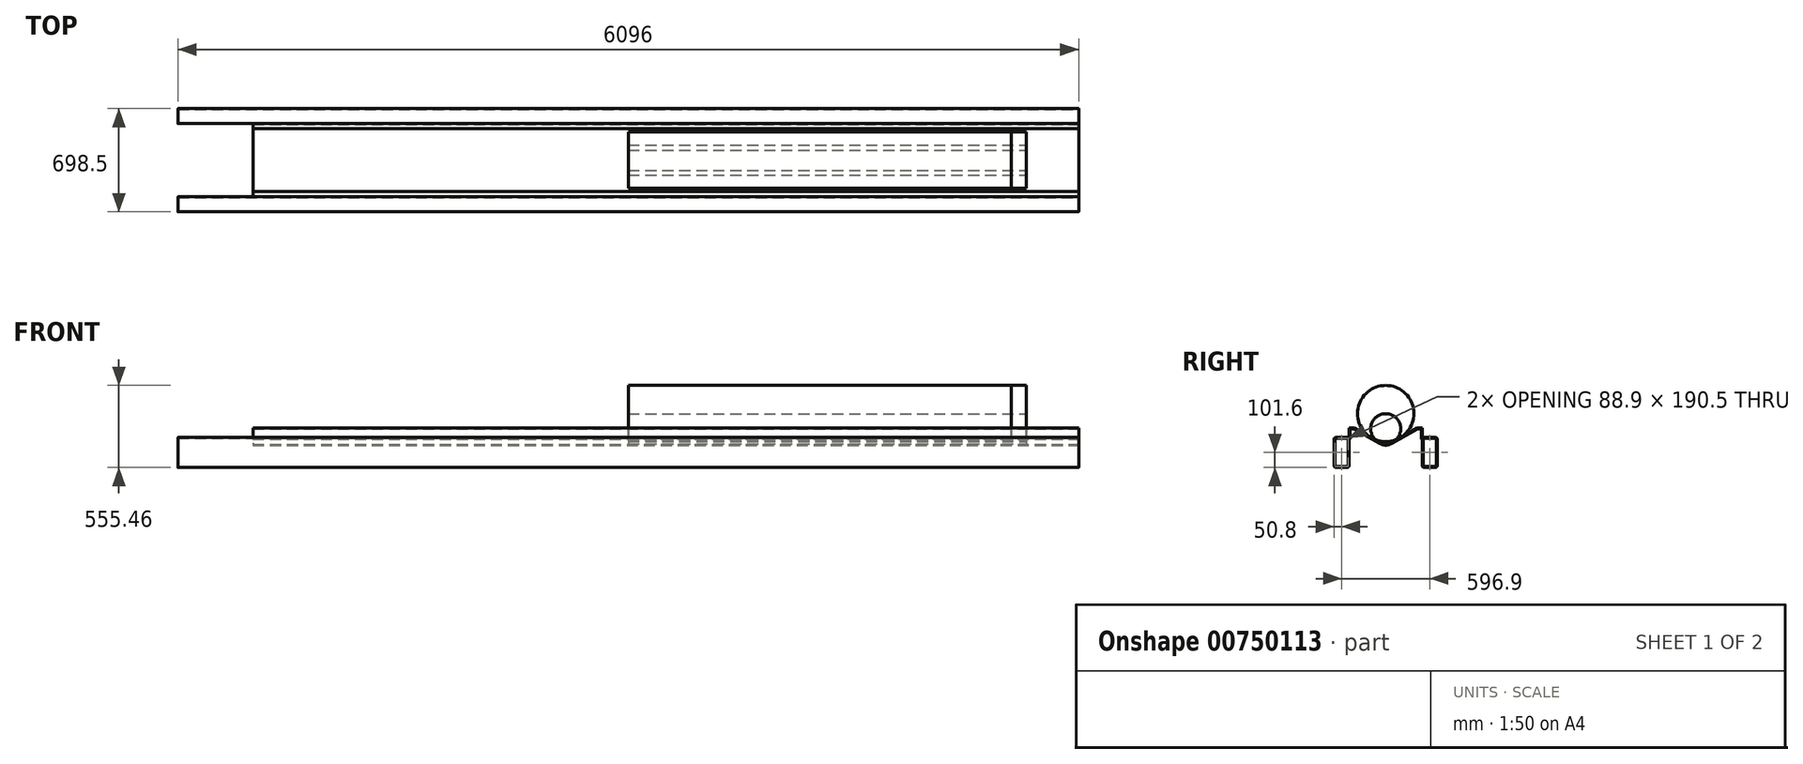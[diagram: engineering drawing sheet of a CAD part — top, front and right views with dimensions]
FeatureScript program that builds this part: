
annotation { "Feature Type Name" : "Feature", "Feature Type Description" : "" }
export const myFeature = defineFeature(function(context is Context, id is Id, definition is map)
    precondition{}
    {
        {
            var Q0;
            Q0=qCreatedBy(makeId("Right.planeOp"),FACE);
            var sketch = newSketch(context, id + "F0", { "sketchPlane" : qUnion([Q0])});
            skPoint(sketch, "E0", {"position": v(0, 0) * mm});
            skLineSegment(sketch, "E1", {"start": v(0, 228.65) * mm, "end": v(0, -305.7) * mm, "construction": true});
            skLineSegment(sketch, "E2.bottom", {"start": v(-336.55, 57.15) * mm, "end": v(-260.35, 57.15) * mm});
            skLineSegment(sketch, "E2.top", {"start": v(-336.55, -146.05) * mm, "end": v(-260.35, -146.05) * mm});
            skLineSegment(sketch, "E2.left", {"start": v(-349.25, 44.45) * mm, "end": v(-349.25, -133.35) * mm});
            skLineSegment(sketch, "E2.right", {"start": v(-247.65, 44.45) * mm, "end": v(-247.65, -133.35) * mm});
            skPoint(sketch, "E3.visualSharp", {"position": v(-247.65, 57.15) * mm});
            skArc(sketch, "E3.filletArc", {"start": v(-247.65, 44.45) * mm, "mid": v(-251.37, 53.43) * mm, "end": v(-260.35, 57.15) * mm});
            skPoint(sketch, "E4.visualSharp", {"position": v(-349.25, -146.05) * mm});
            skArc(sketch, "E4.filletArc", {"start": v(-349.25, -133.35) * mm, "mid": v(-345.53, -142.33) * mm, "end": v(-336.55, -146.05) * mm});
            skPoint(sketch, "E5.visualSharp", {"position": v(-247.65, -146.05) * mm});
            skArc(sketch, "E5.filletArc", {"start": v(-260.35, -146.05) * mm, "mid": v(-251.37, -142.33) * mm, "end": v(-247.65, -133.35) * mm});
            skPoint(sketch, "E6.visualSharp", {"position": v(-349.25, 57.15) * mm});
            skArc(sketch, "E6.filletArc", {"start": v(-336.55, 57.15) * mm, "mid": v(-345.53, 53.43) * mm, "end": v(-349.25, 44.45) * mm});
            skLineSegment(sketch, "E7.MirrorCS", {"start": v(247.65, 44.45) * mm, "end": v(247.65, -133.35) * mm});
            skArc(sketch, "E8.MirrorCS", {"start": v(247.65, 44.45) * mm, "mid": v(251.37, 53.43) * mm, "end": v(260.35, 57.15) * mm});
            skLineSegment(sketch, "E9.MirrorCS", {"start": v(336.55, 57.15) * mm, "end": v(260.35, 57.15) * mm});
            skArc(sketch, "E10.MirrorCS", {"start": v(336.55, 57.15) * mm, "mid": v(345.53, 53.43) * mm, "end": v(349.25, 44.45) * mm});
            skLineSegment(sketch, "E11.MirrorCS", {"start": v(349.25, 44.45) * mm, "end": v(349.25, -133.35) * mm});
            skArc(sketch, "E12.MirrorCS", {"start": v(349.25, -133.35) * mm, "mid": v(345.53, -142.33) * mm, "end": v(336.55, -146.05) * mm});
            skLineSegment(sketch, "E13.MirrorCS", {"start": v(336.55, -146.05) * mm, "end": v(260.35, -146.05) * mm});
            skPoint(sketch, "E14.MirrorP", {"position": v(247.65, -146.05) * mm});
            skArc(sketch, "E15.MirrorCS", {"start": v(260.35, -146.05) * mm, "mid": v(251.37, -142.33) * mm, "end": v(247.65, -133.35) * mm});
            skPoint(sketch, "E16.MirrorP", {"position": v(247.65, 57.15) * mm});
            skLineSegment(sketch, "E17", {"start": v(-213.12, 120.65) * mm, "end": v(-37.54, 21.25) * mm});
            skLineSegment(sketch, "E18.MirrorCS", {"start": v(213.12, 120.65) * mm, "end": v(37.54, 21.25) * mm});
            skLineSegment(sketch, "E19", {"start": v(-364.25, 120.65) * mm, "end": v(0, 120.65) * mm, "construction": true});
            skCircle(sketch, "E20", {"center": v(0, 218.9) * mm, "radius": 190.5 * mm});
            skArc(sketch, "E21.filletArc", {"start": v(-37.54, 21.25) * mm, "mid": v(0, 11.36) * mm, "end": v(37.54, 21.25) * mm});
            skCircle(sketch, "E22", {"center": v(0, 116.75) * mm, "radius": 101.6 * mm});
            skCircle(sketch, "E23", {"center": v(0, 61.3) * mm, "radius": 50.8 * mm, "construction": true});
            skArc(sketch, "E24.0", {"start": v(-336.55, 50.8) * mm, "mid": v(-341.04, 48.94) * mm, "end": v(-342.9, 44.45) * mm});
            skLineSegment(sketch, "E24.1", {"start": v(-342.9, 44.45) * mm, "end": v(-342.9, -133.35) * mm});
            skLineSegment(sketch, "E24.2", {"start": v(-336.55, 50.8) * mm, "end": v(-260.35, 50.8) * mm});
            skArc(sketch, "E24.3", {"start": v(-342.9, -133.35) * mm, "mid": v(-341.04, -137.84) * mm, "end": v(-336.55, -139.7) * mm});
            skArc(sketch, "E24.4", {"start": v(-254, 44.45) * mm, "mid": v(-255.86, 48.94) * mm, "end": v(-260.35, 50.8) * mm});
            skLineSegment(sketch, "E24.5", {"start": v(-254, 44.45) * mm, "end": v(-254, -133.35) * mm});
            skArc(sketch, "E24.6", {"start": v(-260.35, -139.7) * mm, "mid": v(-255.86, -137.84) * mm, "end": v(-254, -133.35) * mm});
            skLineSegment(sketch, "E24.7", {"start": v(-336.55, -139.7) * mm, "end": v(-260.35, -139.7) * mm});
            skArc(sketch, "E25.0", {"start": v(336.55, 50.8) * mm, "mid": v(341.04, 48.94) * mm, "end": v(342.9, 44.45) * mm});
            skLineSegment(sketch, "E25.1", {"start": v(342.9, 44.45) * mm, "end": v(342.9, -133.35) * mm});
            skLineSegment(sketch, "E25.2", {"start": v(336.55, 50.8) * mm, "end": v(260.35, 50.8) * mm});
            skArc(sketch, "E25.3", {"start": v(342.9, -133.35) * mm, "mid": v(341.04, -137.84) * mm, "end": v(336.55, -139.7) * mm});
            skArc(sketch, "E25.4", {"start": v(254, 44.45) * mm, "mid": v(255.86, 48.94) * mm, "end": v(260.35, 50.8) * mm});
            skLineSegment(sketch, "E25.5", {"start": v(254, 44.45) * mm, "end": v(254, -133.35) * mm});
            skArc(sketch, "E25.6", {"start": v(260.35, -139.7) * mm, "mid": v(255.86, -137.84) * mm, "end": v(254, -133.35) * mm});
            skLineSegment(sketch, "E25.7", {"start": v(336.55, -139.7) * mm, "end": v(260.35, -139.7) * mm});
            skLineSegment(sketch, "E26", {"start": v(-278.75, 57.15) * mm, "end": v(-269.35, 57.15) * mm});
            skLineSegment(sketch, "E27", {"start": v(-278.75, 57.15) * mm, "end": v(-268.14, 57.15) * mm});
            skLineSegment(sketch, "E28", {"start": v(-213.12, 120.65) * mm, "end": v(-247.65, 120.65) * mm});
            skLineSegment(sketch, "E29", {"start": v(-247.65, 120.65) * mm, "end": v(-247.65, 44.45) * mm});
            skLineSegment(sketch, "E30.MirrorCS", {"start": v(247.65, 120.65) * mm, "end": v(247.65, 44.45) * mm});
            skLineSegment(sketch, "E31", {"start": v(213.12, 120.65) * mm, "end": v(247.65, 120.65) * mm});
            skLineSegment(sketch, "E32.0", {"start": v(241.3, 114.3) * mm, "end": v(241.3, 44.45) * mm});
            skLineSegment(sketch, "E32.1", {"start": v(-216.25, 115.12) * mm, "end": v(-40.67, 15.73) * mm});
            skArc(sketch, "E32.2", {"start": v(-40.67, 15.73) * mm, "mid": v(0, 5.01) * mm, "end": v(40.67, 15.73) * mm});
            skLineSegment(sketch, "E32.3", {"start": v(214.8, 114.3) * mm, "end": v(40.67, 15.73) * mm});
            skLineSegment(sketch, "E32.4", {"start": v(214.8, 114.3) * mm, "end": v(241.3, 114.3) * mm});
            skLineSegment(sketch, "E33.MirrorCS", {"start": v(-241.3, 114.3) * mm, "end": v(-241.3, 44.45) * mm});
            skLineSegment(sketch, "E34.MirrorCS", {"start": v(-214.8, 114.3) * mm, "end": v(-241.3, 114.3) * mm});
            skLineSegment(sketch, "E35", {"start": v(-241.3, 44.45) * mm, "end": v(-247.65, 44.45) * mm});
            skLineSegment(sketch, "E36", {"start": v(241.3, 44.45) * mm, "end": v(247.65, 44.45) * mm});
            skSolve(sketch);
        }
        {
            var Q0;
            Q0=makeQuery(id+"F0.imprint","IMPRINT",FACE,{"disambiguationData":[TD([[makeQuery(id+"F0.imprint","IMPRINT",EDGE,{"derivedFrom":sQuery(id+"F0.wireOp",EDGE,"E2.top")}),1.0]])]});
            var Q1;
            Q1=makeQuery(id+"F0.imprint","IMPRINT",FACE,{"disambiguationData":[TD([[makeQuery(id+"F0.imprint","IMPRINT",EDGE,{"derivedFrom":sQuery(id+"F0.wireOp",EDGE,"E7.MirrorCS")}),1.0]])]});
            extrude(context, id + "F1", {"entities" : qUnion([Q0, Q1]), "oppositeDirection" : true, "depth" : 6096 * mm, "offsetDistance" : 25.4 * mm});
        }
        {
            var Q0;
            Q0=makeQuery(id+"F0.imprint","IMPRINT",FACE,{"disambiguationData":[TD([[makeQuery(id+"F0.imprint","IMPRINT",EDGE,{"derivedFrom":sQuery(id+"F0.wireOp",EDGE,"E17")}),-1.0]])]});
            var Q1;
            {var subQ4=sQuery(id+"F0.wireOp",EDGE,"40Ta9XpO-4Bih-OJ3X-wqKm-lZXZA3K83W1n");Q1=makeQuery(id+"F0.imprint","IMPRINT",FACE,{"disambiguationData":[TD([[makeQuery(id+"F0.imprint","IMPRINT",EDGE,{"derivedFrom":subQ4}),1.0]])]});}
            var Q2;
            {var subQ0=sQuery(id+"F0.wireOp",EDGE,"hLX8c9pQ-herN-AtC7-Xv8B-rJKkOfKo46Fv");Q2=makeQuery(id+"F0.imprint","IMPRINT",FACE,{"disambiguationData":[TD([[makeQuery(id+"F0.imprint","IMPRINT",EDGE,{"derivedFrom":subQ0}),-1.0]])]});}
            extrude(context, id + "F2", {"entities" : qUnion([Q0, Q1, Q2]), "oppositeDirection" : true, "depth" : 5588 * mm, "offsetDistance" : 25.4 * mm});
        }
        {
            var Q0;
            {var subQ0=sQuery(id+"F0.wireOp",EDGE,"E22");var subQ1=makeQuery(id+"F0.imprint","INTERSECT",VERTEX,{"derivedFrom":[sQuery(id+"F0.wireOp",EDGE,"E17"),subQ0]});Q0=makeQuery(id+"F0.imprint","IMPRINT",FACE,{"disambiguationData":[TD([[makeQuery(id+"F0.imprint","IMPRINT",EDGE,{"disambiguationData":[TD([[subQ1,-1.0]])],"derivedFrom":subQ0}),1.0]])]});}
            var Q1;
            {var subQ0=sQuery(id+"F0.wireOp",EDGE,"E22");var subQ1=sQuery(id+"F0.wireOp",EDGE,"E20");var subQ2=makeQuery(id+"F0.imprint","INTERSECT",VERTEX,{"disambiguationData":[OD(0.0)],"derivedFrom":[subQ1,subQ0]});Q1=makeQuery(id+"F0.imprint","IMPRINT",FACE,{"disambiguationData":[TD([[makeQuery(id+"F0.imprint","IMPRINT",EDGE,{"disambiguationData":[TD([[subQ2,-1.0]])],"derivedFrom":subQ1}),1.0]])]});}
            extrude(context, id + "F3", {"entities" : qUnion([Q0, Q1]), "oppositeDirection" : true, "depth" : 3048 * mm, "offsetDistance" : 25.4 * mm, "hasSecondDirection" : true, "secondDirectionOppositeDirection" : true, "secondDirectionDepth" : 355.6 * mm});
        }
        {
            var Q0;
            {var subQ0=sQuery(id+"F0.wireOp",EDGE,"E20");var subQ1=makeQuery(id+"F0.imprint","INTERSECT",VERTEX,{"derivedFrom":[sQuery(id+"F0.wireOp",EDGE,"E17"),subQ0]});Q0=makeQuery(id+"F0.imprint","IMPRINT",FACE,{"disambiguationData":[TD([[makeQuery(id+"F0.imprint","IMPRINT",EDGE,{"disambiguationData":[TD([[subQ1,-1.0]])],"derivedFrom":subQ0}),1.0]])]});}
            var Q1;
            {var subQ0=sQuery(id+"F0.wireOp",EDGE,"E22");var subQ1=sQuery(id+"F0.wireOp",EDGE,"E20");var subQ2=makeQuery(id+"F0.imprint","INTERSECT",VERTEX,{"disambiguationData":[OD(0.0)],"derivedFrom":[subQ1,subQ0]});Q1=makeQuery(id+"F0.imprint","IMPRINT",FACE,{"disambiguationData":[TD([[makeQuery(id+"F0.imprint","IMPRINT",EDGE,{"disambiguationData":[TD([[subQ2,-1.0]])],"derivedFrom":subQ1}),1.0]])]});}
            extrude(context, id + "F4", {"entities" : qUnion([Q0, Q1]), "oppositeDirection" : true, "depth" : 3048 * mm, "offsetDistance" : 25.4 * mm, "hasSecondDirection" : true, "secondDirectionOppositeDirection" : true, "secondDirectionDepth" : 457.2 * mm});
        }
    });
